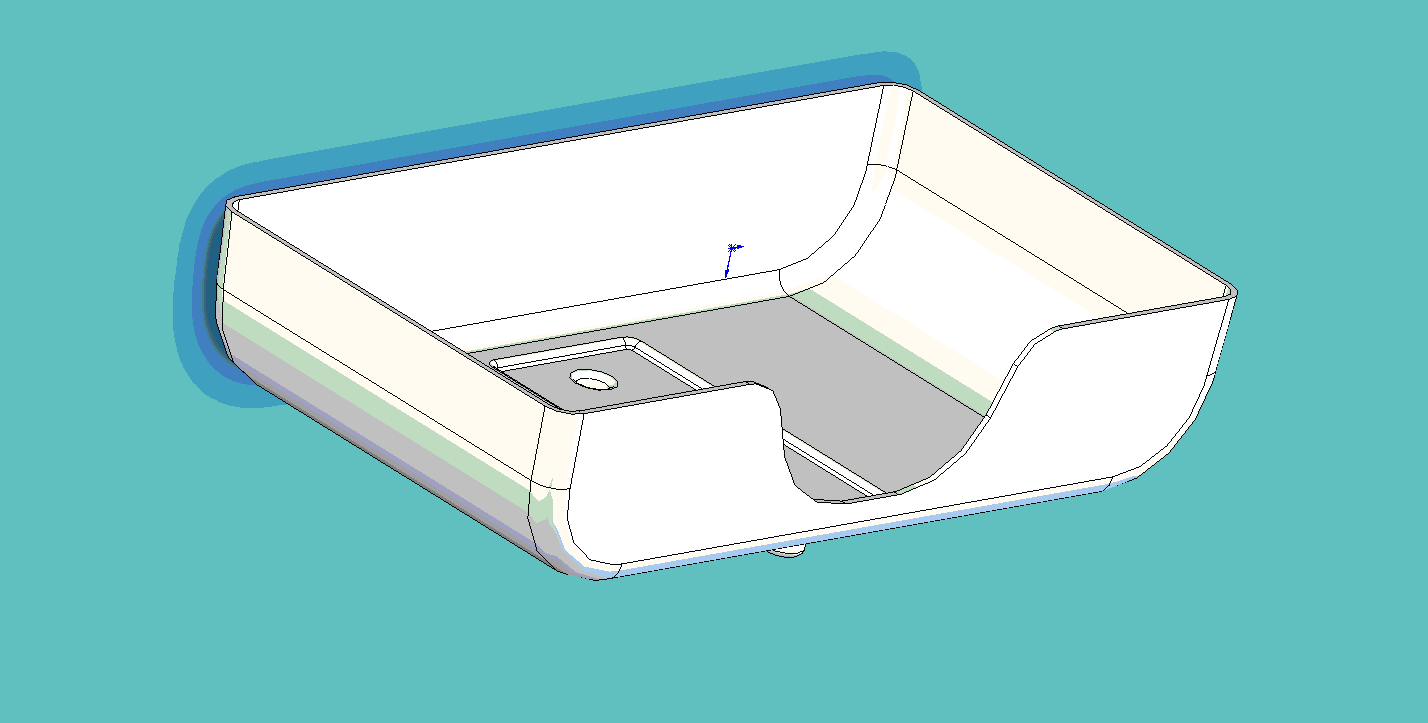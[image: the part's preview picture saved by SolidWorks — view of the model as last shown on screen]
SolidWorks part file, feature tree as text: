
SOLIDWORKS PART (.sldprt)
format: sldprt  version: not decoded by parser v0  size: 658,432 bytes
history: native  units: mm
features: fillet x8, sketch x5, plane x3, extrude x2, cut_extrude x2, material x1, mirror x1, revolve x1, pattern_linear x1, shell x1 (+10 scaffold rows collapsed)
feature tree (35):
  scaffold x10  (default folders/planes/origin — collapsed)
  material  "PVC rigide"
  plane  "Plan de face"
  plane  "Plan de dessus"
  plane  "Plan de droite"
  sketch  "Esquisse1"  dims[c1.D5=35.5mm c1.D2=36.0mm c1.D1=263.0mm c2.D2=24.5mm c2.D3=260.0mm c2.D4=60.0mm c2.D5=188.0mm c2.D6=24.0mm]
  extrude  "Extrusion1"  Depth=153mm
  sketch  "Esquisse2"  dims[D1=52.0mm D2=148.0mm]
  cut_extrude  "Enlèv. mat.-Extru.3"  Depth=300mm
  mirror  "Symétrie1"
  fillet  "Congé1"  Radius=8mm
  sketch  "Esquisse3"  dims[D1=57.0mm D2=28.5mm D3=60.0mm D4=120.0mm]
  extrude  "Extrusion2"  Depth=2.5mm
  fillet  "Congé2"  Radius=4mm
  sketch  "Esquisse4"  dims[c1.D1=13.0mm c1.D2=13.0mm c1.D3=14.0mm c1.D4=119.3mm c2.D1=1.0mm c2.D2=2.0mm c2.D3=13.0mm c2.D5=14.0mm c2.D6=13.0mm]
  revolve  "Révolution1"  Angle=360deg
  pattern_linear  "Répétition linéaire1"  Count1=2 Count2=1 Spacing1=85.6mm Spacing2=50mm
  shell  "Coque1"  Thickness=2mm
  fillet  "Congé3"  Radius=1mm
  fillet  "Congé4"  Radius=2mm
  fillet  "Congé5"  Radius=1mm
  fillet  "Congé6"  Radius=1mm
  fillet  "Congé7"  Radius=2mm
  fillet  "Congé8"  Radius=2mm
  sketch  "Esquisse5"  dims[c1.D6=~31.633079mm c1.D7=~15.548462mm c1.D1=20.0mm c1.D2=91.0mm c1.D3=120.0mm c1.D4=79.0mm c1.D5=15.5mm c2.D6=~9.935559mm c2.D8=~9.935559mm]
  cut_extrude  "Enlèv. mat.-Extru.4"  [1 undecoded]
decode coverage: 19 of 21 modeling features carry decoded parameters
note: ~ marks probable driven/reference dimensions
note: 1 parameter value undecoded
note: suppression state not decoded; provenance and decode notes live in map.json
